# Revit family: pk-rp40_112(la)ka17_50Hz
name_source: partatom
category: 機械設備
units: mm (PartAtom-declared; Revit-internal decimal feet)

## family parameters
OmniClass タイトル = Split System Air Conditioning Units
OmniClass 番号 = 23.75.10.24.21.27.27
パーツ タイプ = 標準
ロード時にボイドで切り取り = いいえ
丸型コネクタ寸法 = 直径を使用
作業面ベース = いいえ
共有 = いいえ
常に垂直 = はい
部屋計算ポイント = はい

## types (8) — shared parameters
Clearance Back = 0 mm
Clearance Bottom = 1800 mm
Clearance Front = 1500 mm
IfcExportAs = IfcUnitaryEquipmentType
IfcExportType = AIRCONDITIONINGUNIT
OmniClassCode = 23-33 17 13 11
Space Bot_1 = 7 mm
URL = https://www.mitsubishielectric.co.jp
Uniclass2015Code = Pr_70_65_03_84
Uniclass2015Title = Split coil remote air cooled condensing units
Uniclass2015Version = Systems v1.9
ケーブルサイズ = 0 mm
サービススペース = はい
ドレン管径 = 16.00 mm
ドレン管径 (外径) = 22 mm
パネルマテリアル = <カテゴリ別>
仕様書バージョン = Version1.0
企業コード = 108420
冷媒管径 = 100.00 mm
冷媒高低圧ガス管径 = 0.00 mm
分類コード = 50053003123070
加湿給水管径 = 0.00 mm
参照している仕様書等のバージョン = 公共建築工事標準仕様書（機械設備工事編）平成31年度版
吊りボルト_H = 0 mm
吊り位置X = 0 mm
吊り位置Y = 0 mm
周波数 = 50 Hz
呼称 = 室内機_壁掛（露出）形
形式 = 壁掛（露出）形
推奨ブレーカー容量 = 0 A
本体マテリアル = <カテゴリ別>
極数 = 1
法定耐用年数 = 6
消費電力_加湿器 = 0.00 kW
消費電力_電気ヒーター = 0.00 kW
発停方法 = 付属スイッチ
相 = 1
積算_科目 = 1 空気調和設備
符号 = PAC_WR
製品リリース年月 = 2021/05/10
製品出荷対象 = 国内
製造元 = 三菱電機株式会社
設置方法 = 壁掛形
設計冷房能力 = 0 kW
設計冷房能力_顕熱 = 0 kW
設計暖房能力 = 0.00 kW
説明 = 店舗・事務所用パッケージエアコン(Mr.SLIM) 壁掛形<ワイヤード>
負荷分類 = 3_ファン類
運転質量 = 0.00 kg
電圧 = 200 V
電圧_電気ヒーター = 0 V
電源_H = 0 mm
zero-valued in all types: 有効加湿量

## per-type parameters (varying)
- 壁掛_PK-RP45LA: Clearance Left=50 mm; Clearance Right=150 mm; Clearance Top=50 mm; Depth=237 mm; Height=299 mm; MAX風量=642.0 m³/h; MID風量=564.0 m³/h; MIN風量=492.0 m³/h; S_H=356 mm; Space Bot_2=250 mm; Space Left=50 mm; Space Right=150 mm; Space Right_1=260 mm; Space Top=50 mm; Width=898 mm; サービススペース PK-RP40LA～PK-RP50LA / PK-RP80KA～PK-RP112KA=はい; サービススペース PK-RP56KA～PK-RP71KA=いいえ; ドレン位置-X=660 mm; ドレン位置-Y=35 mm; ドレン位置-Z=245 mm; 価格=213000 $; 冷媒ガス管位置-X=642 mm; 冷媒ガス管位置-Y=35 mm; 冷媒ガス管位置-Z=268 mm; 冷媒ガス管径=12.70 mm; 冷媒液管位置-X=711 mm; 冷媒液管位置-Y=35 mm; 冷媒液管位置-Z=280 mm; 冷媒液管径=6.35 mm; 冷媒管径符号=Ac; 冷房能力=4 kW; 壁掛_PK-RP40_50LA=はい; 壁掛_PK-RP56_71KA17=いいえ; 壁掛_PK-RP80_112KA17=いいえ; 始動方式=直⼊; 暖房能力=4.50 kW; 構成品番=PK-RP45LA; 消費電力=0.04 kW; 消費電力_冷房=0.04 kW; 消費電力_暖房=0.03 kW; 製品質量=12.50 kg; 質量=15.00 kg; 電動機出力_送風機=0.03 kW; 音響パワーレベル(dB)=57; 音響パワーレベル（中）(dB)=54; 音響パワーレベル（弱）(dB)=51; 音響パワーレベル（静）(dB)=48; 風量=642.0 m³/h; 風量_中 (m3/min)=9.4; 風量_弱 (m3/min)=8.2; 風量_強 (m3/min)=10.7; 風量_静 (m3/min)=6.8
- 壁掛_PK-RP50LA: Clearance Left=50 mm; Clearance Right=150 mm; Clearance Top=50 mm; Depth=237 mm; Height=299 mm; MAX風量=642.0 m³/h; MID風量=564.0 m³/h; MIN風量=492.0 m³/h; S_H=356 mm; Space Bot_2=250 mm; Space Left=50 mm; Space Right=150 mm; Space Right_1=260 mm; Space Top=50 mm; Width=898 mm; サービススペース PK-RP40LA～PK-RP50LA / PK-RP80KA～PK-RP112KA=はい; サービススペース PK-RP56KA～PK-RP71KA=いいえ; ドレン位置-X=660 mm; ドレン位置-Y=35 mm; ドレン位置-Z=245 mm; 価格=251000 $; 冷媒ガス管位置-X=642 mm; 冷媒ガス管位置-Y=35 mm; 冷媒ガス管位置-Z=268 mm; 冷媒ガス管径=12.70 mm; 冷媒液管位置-X=711 mm; 冷媒液管位置-Y=35 mm; 冷媒液管位置-Z=280 mm; 冷媒液管径=6.35 mm; 冷媒管径符号=Ac; 冷房能力=4.5 kW; 壁掛_PK-RP40_50LA=はい; 壁掛_PK-RP56_71KA17=いいえ; 壁掛_PK-RP80_112KA17=いいえ; 始動方式=直⼊; 暖房能力=5.00 kW; 構成品番=PK-RP50LA; 消費電力=0.04 kW; 消費電力_冷房=0.04 kW; 消費電力_暖房=0.03 kW; 製品質量=12.50 kg; 質量=15.00 kg; 電動機出力_送風機=0.03 kW; 音響パワーレベル(dB)=57; 音響パワーレベル（中）(dB)=54; 音響パワーレベル（弱）(dB)=51; 音響パワーレベル（静）(dB)=48; 風量=642.0 m³/h; 風量_中 (m3/min)=9.4; 風量_弱 (m3/min)=8.2; 風量_強 (m3/min)=10.7; 風量_静 (m3/min)=6.8
- 壁掛_PK-RP40LA: Clearance Left=50 mm; Clearance Right=150 mm; Clearance Top=50 mm; Depth=237 mm; Height=299 mm; MAX風量=642.0 m³/h; MID風量=564.0 m³/h; MIN風量=492.0 m³/h; S_H=356 mm; Space Bot_2=250 mm; Space Left=50 mm; Space Right=150 mm; Space Right_1=260 mm; Space Top=50 mm; Width=898 mm; サービススペース PK-RP40LA～PK-RP50LA / PK-RP80KA～PK-RP112KA=はい; サービススペース PK-RP56KA～PK-RP71KA=いいえ; ドレン位置-X=660 mm; ドレン位置-Y=35 mm; ドレン位置-Z=245 mm; 価格=205000 $; 冷媒ガス管位置-X=642 mm; 冷媒ガス管位置-Y=35 mm; 冷媒ガス管位置-Z=268 mm; 冷媒ガス管径=12.70 mm; 冷媒液管位置-X=711 mm; 冷媒液管位置-Y=35 mm; 冷媒液管位置-Z=280 mm; 冷媒液管径=6.35 mm; 冷媒管径符号=Ac; 冷房能力=3.6 kW; 壁掛_PK-RP40_50LA=はい; 壁掛_PK-RP56_71KA17=いいえ; 壁掛_PK-RP80_112KA17=いいえ; 始動方式=直入; 暖房能力=4.00 kW; 構成品番=PK-RP40LA; 消費電力=0.04 kW; 消費電力_冷房=0.04 kW; 消費電力_暖房=0.03 kW; 製品質量=12.50 kg; 質量=15.00 kg; 電動機出力_送風機=0.03 kW; 音響パワーレベル(dB)=57; 音響パワーレベル（中）(dB)=54; 音響パワーレベル（弱）(dB)=51; 音響パワーレベル（静）(dB)=47; 風量=642.0 m³/h; 風量_中 (m3/min)=9.4; 風量_弱 (m3/min)=8.2; 風量_強 (m3/min)=10.7; 風量_静 (m3/min)=6.8
- 壁掛_PK-RP71KA17: Clearance Left=22 mm; Clearance Right=27 mm; Clearance Top=72 mm; Depth=258 mm; Height=325 mm; MAX風量=1032.0 m³/h; MID風量=816.0 m³/h; MIN風量=564.0 m³/h; S_H=404 mm; Space Bot_2=0 mm; Space Left=22 mm; Space Right=27 mm; Space Right_1=0 mm; Space Top=72 mm; Width=1100 mm; サービススペース PK-RP40LA～PK-RP50LA / PK-RP80KA～PK-RP112KA=いいえ; サービススペース PK-RP56KA～PK-RP71KA=はい; ドレン位置-X=733 mm; ドレン位置-Y=25 mm; ドレン位置-Z=300 mm; 価格=264000 $; 冷媒ガス管位置-X=603 mm; 冷媒ガス管位置-Y=25 mm; 冷媒ガス管位置-Z=270 mm; 冷媒ガス管径=15.88 mm; 冷媒液管位置-X=673 mm; 冷媒液管位置-Y=25 mm; 冷媒液管位置-Z=250 mm; 冷媒液管径=9.52 mm; 冷媒管径符号=Bd; 冷房能力=6.3 kW; 壁掛_PK-RP40_50LA=いいえ; 壁掛_PK-RP56_71KA17=はい; 壁掛_PK-RP80_112KA17=いいえ; 始動方式=直⼊; 暖房能力=7.00 kW; 構成品番=PK-RP71KA17; 消費電力=0.06 kW; 消費電力_冷房=0.06 kW; 消費電力_暖房=0.06 kW; 製品質量=16.00 kg; 質量=19.20 kg; 電動機出力_送風機=0.06 kW; 音響パワーレベル(dB)=62; 音響パワーレベル（中）(dB)=56; 音響パワーレベル（弱）(dB)=49; 音響パワーレベル（静）(dB)=0; 風量=1032.0 m³/h; 風量_中 (m3/min)=13.6; 風量_弱 (m3/min)=9.4; 風量_強 (m3/min)=17.2; 風量_静 (m3/min)=0
- 壁掛_PK-RP80KA17: Clearance Left=52 mm; Clearance Right=101 mm; Clearance Top=48 mm; Depth=295 mm; Height=365 mm; MAX風量=1380.0 m³/h; MID風量=1200.0 m³/h; MIN風量=1020.0 m³/h; S_H=420 mm; Space Bot_2=250 mm; Space Left=52 mm; Space Right=101 mm; Space Right_1=220 mm; Space Top=48 mm; Width=1170 mm; サービススペース PK-RP40LA～PK-RP50LA / PK-RP80KA～PK-RP112KA=はい; サービススペース PK-RP56KA～PK-RP71KA=いいえ; ドレン位置-X=719 mm; ドレン位置-Y=61 mm; ドレン位置-Z=347 mm; 価格=272000 $; 冷媒ガス管位置-X=567 mm; 冷媒ガス管位置-Y=25 mm; 冷媒ガス管位置-Z=333 mm; 冷媒ガス管径=15.88 mm; 冷媒液管位置-X=636 mm; 冷媒液管位置-Y=30 mm; 冷媒液管位置-Z=312 mm; 冷媒液管径=9.52 mm; 冷媒管径符号=Bd; 冷房能力=7.1 kW; 壁掛_PK-RP40_50LA=いいえ; 壁掛_PK-RP56_71KA17=いいえ; 壁掛_PK-RP80_112KA17=はい; 始動方式=直⼊; 暖房能力=8.00 kW; 構成品番=PK-RP80KA17; 消費電力=0.07 kW; 消費電力_冷房=0.07 kW; 消費電力_暖房=0.07 kW; 製品質量=21.00 kg; 質量=25.20 kg; 電動機出力_送風機=0.06 kW; 音響パワーレベル(dB)=61; 音響パワーレベル（中）(dB)=57; 音響パワーレベル（弱）(dB)=53; 音響パワーレベル（静）(dB)=0; 風量=1380.0 m³/h; 風量_中 (m3/min)=20; 風量_弱 (m3/min)=17; 風量_強 (m3/min)=23; 風量_静 (m3/min)=0
- 壁掛_PK-RP56KA17: Clearance Left=22 mm; Clearance Right=27 mm; Clearance Top=72 mm; Depth=258 mm; Height=325 mm; MAX風量=1032.0 m³/h; MID風量=816.0 m³/h; MIN風量=564.0 m³/h; S_H=404 mm; Space Bot_2=0 mm; Space Left=22 mm; Space Right=27 mm; Space Right_1=0 mm; Space Top=72 mm; Width=1100 mm; サービススペース PK-RP40LA～PK-RP50LA / PK-RP80KA～PK-RP112KA=いいえ; サービススペース PK-RP56KA～PK-RP71KA=はい; ドレン位置-X=733 mm; ドレン位置-Y=25 mm; ドレン位置-Z=300 mm; 価格=262000 $; 冷媒ガス管位置-X=603 mm; 冷媒ガス管位置-Y=25 mm; 冷媒ガス管位置-Z=270 mm; 冷媒ガス管径=12.70 mm; 冷媒液管位置-X=673 mm; 冷媒液管位置-Y=25 mm; 冷媒液管位置-Z=250 mm; 冷媒液管径=6.35 mm; 冷媒管径符号=Ac; 冷房能力=5 kW; 壁掛_PK-RP40_50LA=いいえ; 壁掛_PK-RP56_71KA17=はい; 壁掛_PK-RP80_112KA17=いいえ; 始動方式=直⼊; 暖房能力=5.60 kW; 構成品番=PK-RP56KA17; 消費電力=0.06 kW; 消費電力_冷房=0.06 kW; 消費電力_暖房=0.06 kW; 製品質量=16.00 kg; 質量=19.20 kg; 電動機出力_送風機=0.06 kW; 音響パワーレベル(dB)=62; 音響パワーレベル（中）(dB)=56; 音響パワーレベル（弱）(dB)=49; 音響パワーレベル（静）(dB)=0; 風量=1032.0 m³/h; 風量_中 (m3/min)=13.6; 風量_弱 (m3/min)=9.4; 風量_強 (m3/min)=17.2; 風量_静 (m3/min)=0
- 壁掛_PK-RP63KA17: Clearance Left=22 mm; Clearance Right=27 mm; Clearance Top=72 mm; Depth=258 mm; Height=325 mm; MAX風量=1032.0 m³/h; MID風量=816.0 m³/h; MIN風量=564.0 m³/h; S_H=404 mm; Space Bot_2=0 mm; Space Left=22 mm; Space Right=27 mm; Space Right_1=0 mm; Space Top=72 mm; Width=1100 mm; サービススペース PK-RP40LA～PK-RP50LA / PK-RP80KA～PK-RP112KA=いいえ; サービススペース PK-RP56KA～PK-RP71KA=はい; ドレン位置-X=733 mm; ドレン位置-Y=25 mm; ドレン位置-Z=300 mm; 価格=263000 $; 冷媒ガス管位置-X=603 mm; 冷媒ガス管位置-Y=25 mm; 冷媒ガス管位置-Z=270 mm; 冷媒ガス管径=12.70 mm; 冷媒液管位置-X=673 mm; 冷媒液管位置-Y=25 mm; 冷媒液管位置-Z=250 mm; 冷媒液管径=6.35 mm; 冷媒管径符号=Ac; 冷房能力=5.6 kW; 壁掛_PK-RP40_50LA=いいえ; 壁掛_PK-RP56_71KA17=はい; 壁掛_PK-RP80_112KA17=いいえ; 始動方式=直⼊; 暖房能力=6.30 kW; 構成品番=PK-RP63KA17; 消費電力=0.06 kW; 消費電力_冷房=0.06 kW; 消費電力_暖房=0.06 kW; 製品質量=16.00 kg; 質量=19.20 kg; 電動機出力_送風機=0.06 kW; 音響パワーレベル(dB)=62; 音響パワーレベル（中）(dB)=56; 音響パワーレベル（弱）(dB)=49; 音響パワーレベル（静）(dB)=0; 風量=1032.0 m³/h; 風量_中 (m3/min)=13.6; 風量_弱 (m3/min)=9.4; 風量_強 (m3/min)=17.2; 風量_静 (m3/min)=0
- 壁掛_PK-RP112KA17: Clearance Left=52 mm; Clearance Right=101 mm; Clearance Top=48 mm; Depth=295 mm; Height=365 mm; MAX風量=1500.0 m³/h; MID風量=1260.0 m³/h; MIN風量=1020.0 m³/h; S_H=420 mm; Space Bot_2=250 mm; Space Left=52 mm; Space Right=101 mm; Space Right_1=220 mm; Space Top=48 mm; Width=1170 mm; サービススペース PK-RP40LA～PK-RP50LA / PK-RP80KA～PK-RP112KA=はい; サービススペース PK-RP56KA～PK-RP71KA=いいえ; ドレン位置-X=719 mm; ドレン位置-Y=61 mm; ドレン位置-Z=347 mm; 価格=280000 $; 冷媒ガス管位置-X=567 mm; 冷媒ガス管位置-Y=25 mm; 冷媒ガス管位置-Z=333 mm; 冷媒ガス管径=15.88 mm; 冷媒液管位置-X=636 mm; 冷媒液管位置-Y=30 mm; 冷媒液管位置-Z=312 mm; 冷媒液管径=9.52 mm; 冷媒管径符号=Bd; 冷房能力=10 kW; 壁掛_PK-RP40_50LA=いいえ; 壁掛_PK-RP56_71KA17=いいえ; 壁掛_PK-RP80_112KA17=はい; 始動方式=直⼊; 暖房能力=11.20 kW; 構成品番=PK-RP112KA17; 消費電力=0.07 kW; 消費電力_冷房=0.07 kW; 消費電力_暖房=0.07 kW; 製品質量=21.00 kg; 質量=25.20 kg; 電動機出力_送風機=0.06 kW; 音響パワーレベル(dB)=66; 音響パワーレベル（中）(dB)=61; 音響パワーレベル（弱）(dB)=56; 音響パワーレベル（静）(dB)=0; 風量=1500.0 m³/h; 風量_中 (m3/min)=21; 風量_弱 (m3/min)=17; 風量_強 (m3/min)=25; 風量_静 (m3/min)=0

## geometry (parser evidence)
native form markers: Sweep x3
no freeform markers — native parametric forms only
